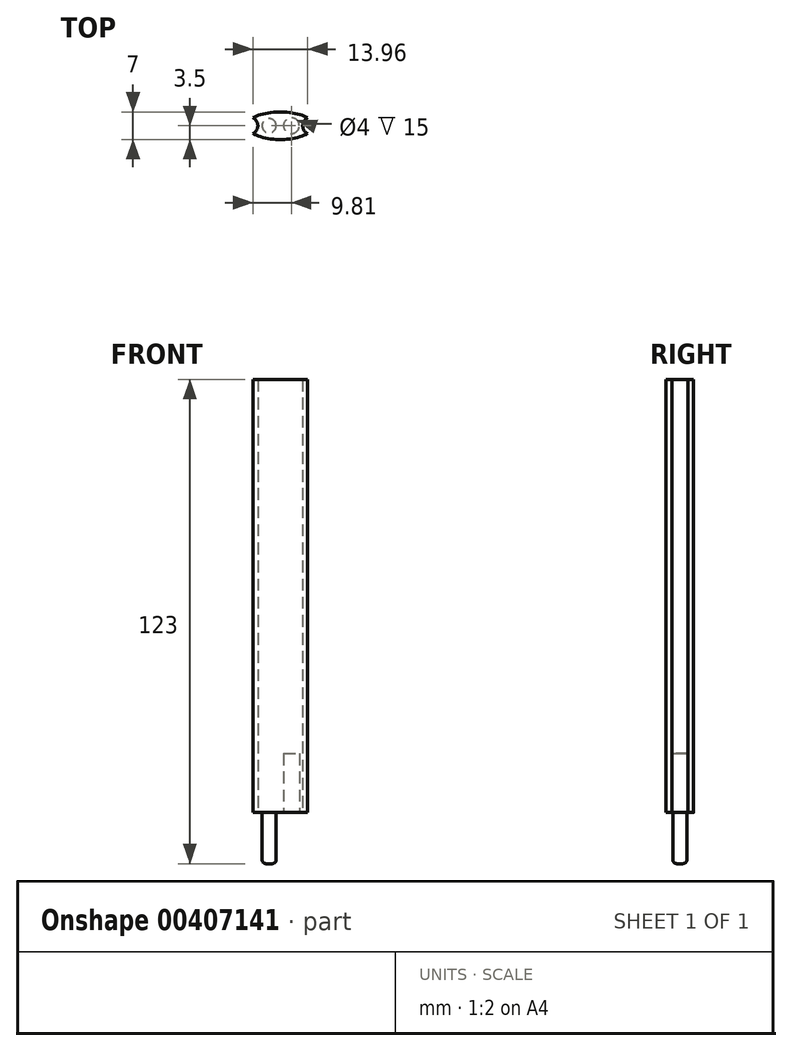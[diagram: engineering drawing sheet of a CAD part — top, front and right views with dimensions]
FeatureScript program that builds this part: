
annotation { "Feature Type Name" : "Feature", "Feature Type Description" : "" }
export const myFeature = defineFeature(function(context is Context, id is Id, definition is map)
    precondition{}
    {
        {
            var Q0;
            Q0=qCreatedBy(makeId("Top.planeOp"),FACE);
            var sketch = newSketch(context, id + "F0", { "sketchPlane" : qUnion([Q0])});
            skLineSegment(sketch, "E0", {"start": v(-10, 0) * mm, "end": v(10, 0) * mm, "construction": true});
            skLineSegment(sketch, "E1", {"start": v(0, -4) * mm, "end": v(0, 4) * mm, "construction": true});
            skEllipticalArc(sketch, "E2", {"construction": true});
            skArc(sketch, "E3", {"start": v(-6.98, -2) * mm, "mid": v(-5.7, 0) * mm, "end": v(-6.98, 2) * mm});
            skArc(sketch, "E4", {"start": v(6.98, 2) * mm, "mid": v(5.7, 0) * mm, "end": v(6.98, -2) * mm});
            skEllipticalArc(sketch, "E5", {});
            skEllipticalArc(sketch, "E6.trimOffspring", {"construction": true});
            skEllipticalArc(sketch, "E7.trimOffspring", {});
            const initialGuessF0  = {"E2": [0, 0, -1, 0, 0.0085, 0.0035, 0.6075302167070781, 2.5340624368827154], "E5": [0, 0, -1, 0, 0.0085, 0.0035, 0.6075302167070781, 2.5340624368827154], "E6.trimOffspring": [0, 0, -1, 0, 0.0085, 0.0035, 3.749122870296872, 5.6756550904725085], "E7.trimOffspring": [0, 0, -1, 0, 0.0085, 0.0035, 3.749122870296872, 5.6756550904725085]};
            skSetInitialGuess(sketch, initialGuessF0);
            skSolve(sketch);
        }
        {
            var Q0;
            Q0=qSketchRegion(id+"F0",true);
            extrude(context, id + "F1", {"entities" : qUnion([Q0]), "depth" : 110 * mm, "offsetDistance" : 25 * mm});
        }
        {
            var Q0;
            Q0=makeQuery(id+"F1.opExtrude","CAP_FACE",FACE,{"disambiguationData":[OSD([sQuery(id+"F0.wireOp",EDGE,"E3"),sQuery(id+"F0.wireOp",EDGE,"E4"),sQuery(id+"F0.wireOp",EDGE,"E5"),sQuery(id+"F0.wireOp",EDGE,"E7.trimOffspring")])],"isStart":true});
            var sketch = newSketch(context, id + "F2", { "sketchPlane" : qUnion([Q0])});
            skLineSegment(sketch, "E8", {"start": v(5.7, 0) * mm, "end": v(-5.7, 0) * mm, "construction": true});
            skCircle(sketch, "E9", {"center": v(2.83, 0) * mm, "radius": 2 * mm});
            skCircle(sketch, "E10", {"center": v(-2.83, 0) * mm, "radius": 1.8 * mm, "construction": true});
            skLineSegment(sketch, "E11", {"start": v(0, 0) * mm, "end": v(0, -2.52) * mm, "construction": true});
            skSolve(sketch);
        }
        {
            var Q0;
            Q0 = qSketchRegion(id + "F2", true);
            extrude(context, id + "F3", {"entities" : qUnion([Q0]), "operationType" : NewBodyOperationType.REMOVE, "oppositeDirection" : true, "depth" : 15 * mm, "offsetDistance" : 25 * mm});
        }
        {
            var Q0;
            Q0=makeQuery(id+"F1.opExtrude","CAP_FACE",FACE,{"disambiguationData":[OSD([sQuery(id+"F0.wireOp",EDGE,"E3"),sQuery(id+"F0.wireOp",EDGE,"E4"),sQuery(id+"F0.wireOp",EDGE,"E5"),sQuery(id+"F0.wireOp",EDGE,"E7.trimOffspring")])],"isStart":true});
            var sketch = newSketch(context, id + "F4", { "sketchPlane" : qUnion([Q0])});
            skCircle(sketch, "E12.0", {"center": v(-2.83, 0) * mm, "radius": 1.8 * mm});
            skSolve(sketch);
        }
        {
            var Q0;
            Q0 = qSketchRegion(id + "F4", true);
            extrude(context, id + "F5", {"entities" : qUnion([Q0]), "operationType" : NewBodyOperationType.ADD, "depth" : 13 * mm, "offsetDistance" : 25 * mm});
        }
        {
            var Q0;
            Q0=makeQuery(id+"F5.opExtrude","CAP_EDGE",EDGE,{"disambiguationData":[OSD([sQuery(id+"F4.wireOp",EDGE,"E12.0")])],"isStart":false});
            fillet(context, id + "F6", {"entities" : qUnion([Q0]), "radius" : 1 * mm, "tangentPropagation" : true, "allowEdgeOverflow" : false});
        }
    });
